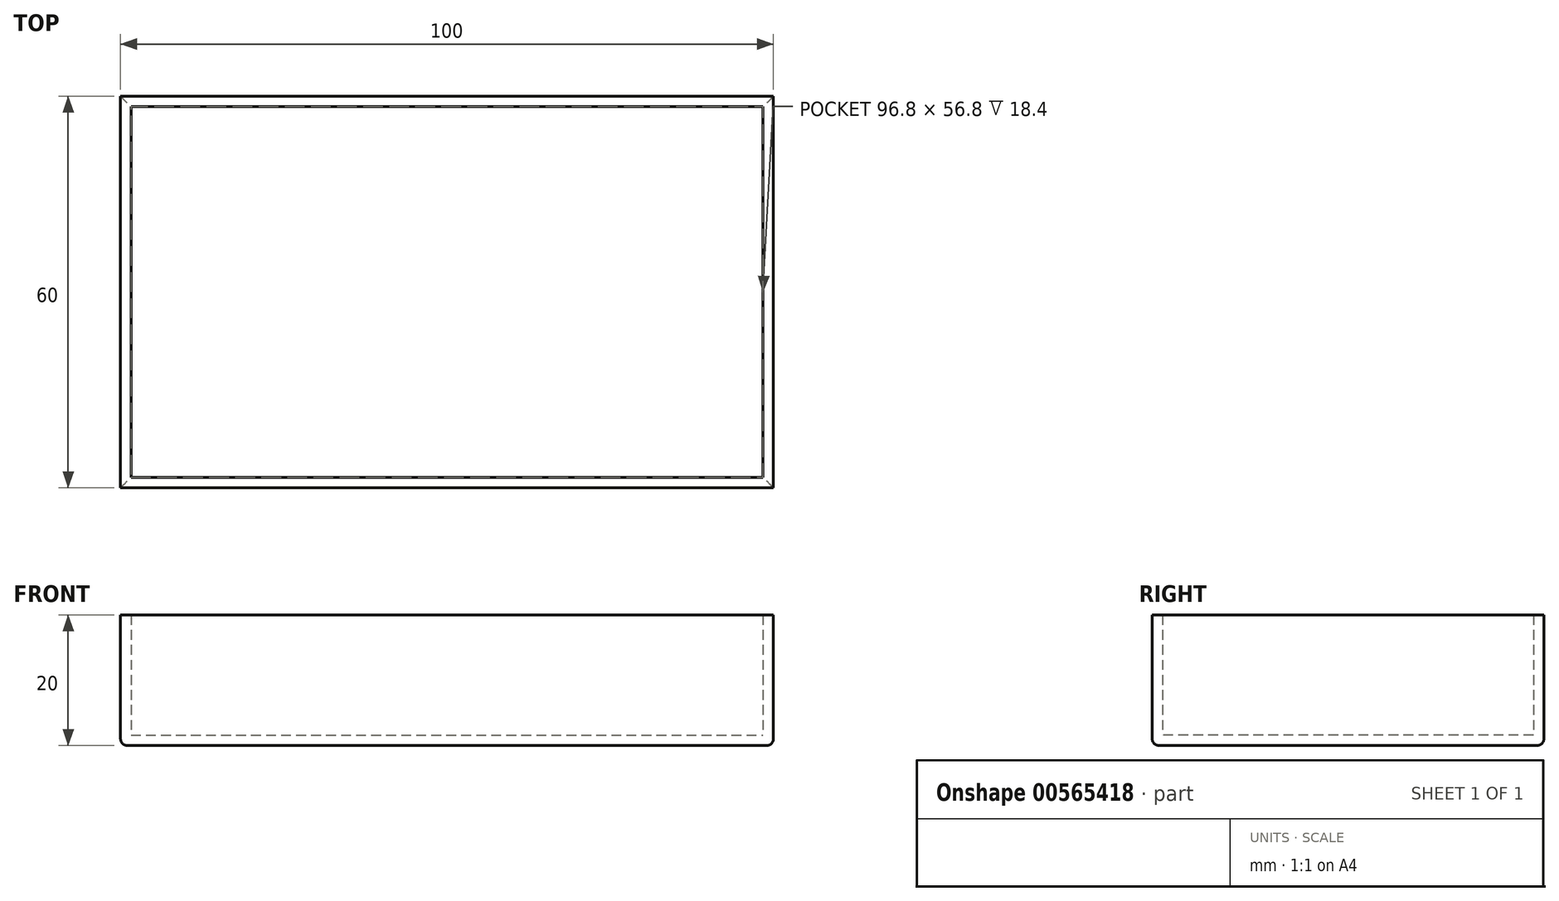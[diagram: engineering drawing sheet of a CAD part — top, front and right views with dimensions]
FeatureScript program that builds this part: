
annotation { "Feature Type Name" : "Feature", "Feature Type Description" : "" }
export const myFeature = defineFeature(function(context is Context, id is Id, definition is map)
    precondition{}
    {
        {
            var Q0;
            Q0=qCreatedBy(makeId("Top.planeOp"),FACE);
            var sketch = newSketch(context, id + "F0", { "sketchPlane" : qUnion([Q0])});
            skLineSegment(sketch, "E0.bottom", {"start": v(-69.47, 33.29) * mm, "end": v(30.53, 33.29) * mm});
            skLineSegment(sketch, "E0.top", {"start": v(-69.47, -26.71) * mm, "end": v(30.53, -26.71) * mm});
            skLineSegment(sketch, "E0.left", {"start": v(-69.47, 33.29) * mm, "end": v(-69.47, -26.71) * mm});
            skLineSegment(sketch, "E0.right", {"start": v(30.53, 33.29) * mm, "end": v(30.53, -26.71) * mm});
            skSolve(sketch);
        }
        {
            var Q0;
            Q0=makeQuery(id+"F0.imprint","IMPRINT",FACE,{"disambiguationData":[TD([[makeQuery(id+"F0.imprint","IMPRINT",EDGE,{"derivedFrom":sQuery(id+"F0.wireOp",EDGE,"E0.bottom")}),-1.0]])]});
            extrude(context, id + "F1", {"entities" : qUnion([Q0]), "depth" : 20 * mm, "offsetDistance" : 25 * mm});
        }
        {
            var Q0;
            Q0=makeQuery(id+"F1.opExtrude","CAP_FACE",FACE,{"disambiguationData":[OSD([sQuery(id+"F0.wireOp",EDGE,"E0.bottom"),sQuery(id+"F0.wireOp",EDGE,"E0.top"),sQuery(id+"F0.wireOp",EDGE,"E0.left"),sQuery(id+"F0.wireOp",EDGE,"E0.right")])],"isStart":false});
            shell(context, id + "F2", {"entities" : qUnion([Q0]), "thickness" : 1.6 * mm});
        }
        {
            var Q0;
            Q0=makeQuery(id+"F1.opExtrude","CAP_EDGE",EDGE,{"disambiguationData":[OSD([sQuery(id+"F0.wireOp",EDGE,"E0.left")])],"isStart":true});
            var Q1;
            Q1=makeQuery(id+"F1.opExtrude","CAP_EDGE",EDGE,{"disambiguationData":[OSD([sQuery(id+"F0.wireOp",EDGE,"E0.top")])],"isStart":true});
            var Q2;
            Q2=makeQuery(id+"F1.opExtrude","CAP_EDGE",EDGE,{"disambiguationData":[OSD([sQuery(id+"F0.wireOp",EDGE,"E0.right")])],"isStart":true});
            var Q3;
            Q3=makeQuery(id+"F1.opExtrude","CAP_EDGE",EDGE,{"disambiguationData":[OSD([sQuery(id+"F0.wireOp",EDGE,"E0.bottom")])],"isStart":true});
            fillet(context, id + "F3", {"entities" : qUnion([Q0, Q1, Q2, Q3]), "radius" : 1 * mm, "tangentPropagation" : true, "allowEdgeOverflow" : false});
        }
    });
